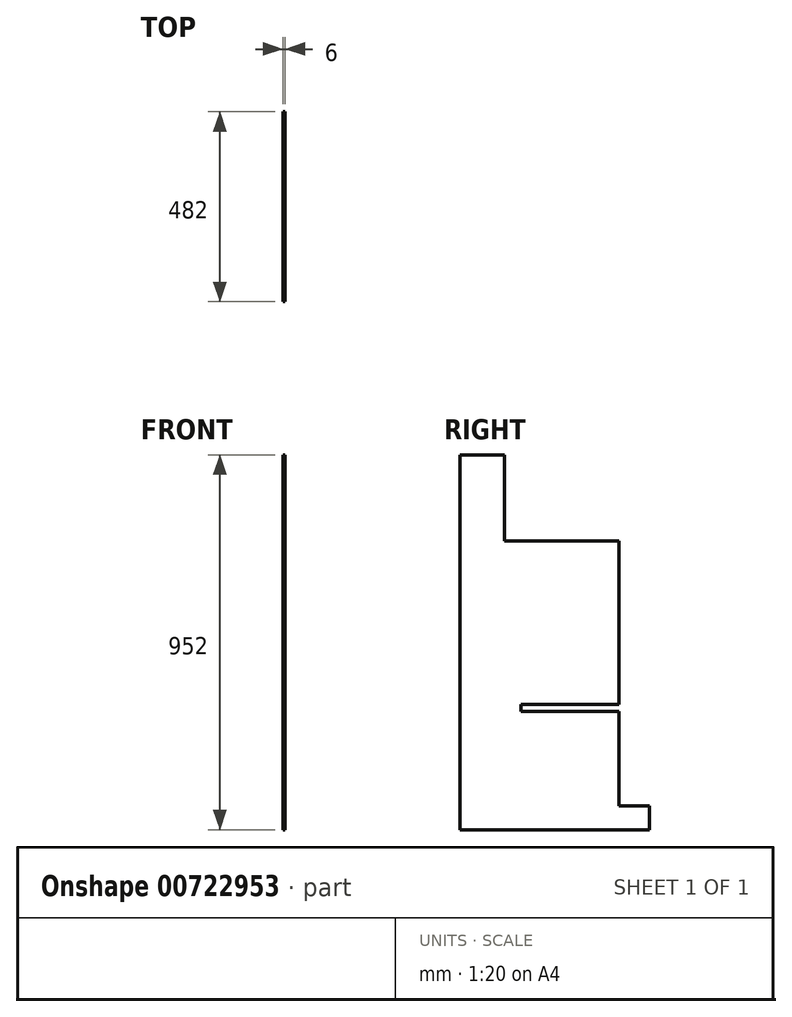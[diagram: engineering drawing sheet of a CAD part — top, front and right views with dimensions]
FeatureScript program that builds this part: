
annotation { "Feature Type Name" : "Feature", "Feature Type Description" : "" }
export const myFeature = defineFeature(function(context is Context, id is Id, definition is map)
    precondition{}
    {
        {
            var Q0;
            Q0=qCreatedBy(makeId("Right.planeOp"),FACE);
            var sketch = newSketch(context, id + "F0", { "sketchPlane" : qUnion([Q0])});
            skLineSegment(sketch, "E0.bottom", {"start": v(-482, 218) * mm, "end": v(-368, 218) * mm});
            skLineSegment(sketch, "E0.top", {"start": v(-482, -734) * mm, "end": v(0, -734) * mm});
            skLineSegment(sketch, "E0.left", {"start": v(-482, 218) * mm, "end": v(-482, -734) * mm});
            skLineSegment(sketch, "E0.right", {"start": v(0, -674) * mm, "end": v(0, -734) * mm});
            skLineSegment(sketch, "E1", {"start": v(-368, 218) * mm, "end": v(-368, 0) * mm});
            skLineSegment(sketch, "E2", {"start": v(-368, 0) * mm, "end": v(-78, 0) * mm});
            skLineSegment(sketch, "E3", {"start": v(-78, 0) * mm, "end": v(-78, -416) * mm});
            skLineSegment(sketch, "E4", {"start": v(-78, -416) * mm, "end": v(-326, -416) * mm});
            skLineSegment(sketch, "E5", {"start": v(-326, -416) * mm, "end": v(-326, -434) * mm});
            skLineSegment(sketch, "E6", {"start": v(-326, -434) * mm, "end": v(-78, -434) * mm});
            skLineSegment(sketch, "E7", {"start": v(-78, -434) * mm, "end": v(-78, -674) * mm});
            skLineSegment(sketch, "E8", {"start": v(-78, -674) * mm, "end": v(-60, -674) * mm});
            skLineSegment(sketch, "E9", {"start": v(-60, -674) * mm, "end": v(0, -674) * mm});
            skSolve(sketch);
        }
        {
            var Q0;
            Q0=qSketchRegion(id+"F0",true);
            extrude(context, id + "F1", {"entities" : qUnion([Q0]), "depth" : 6 * mm, "offsetDistance" : 25 * mm});
        }
    });
